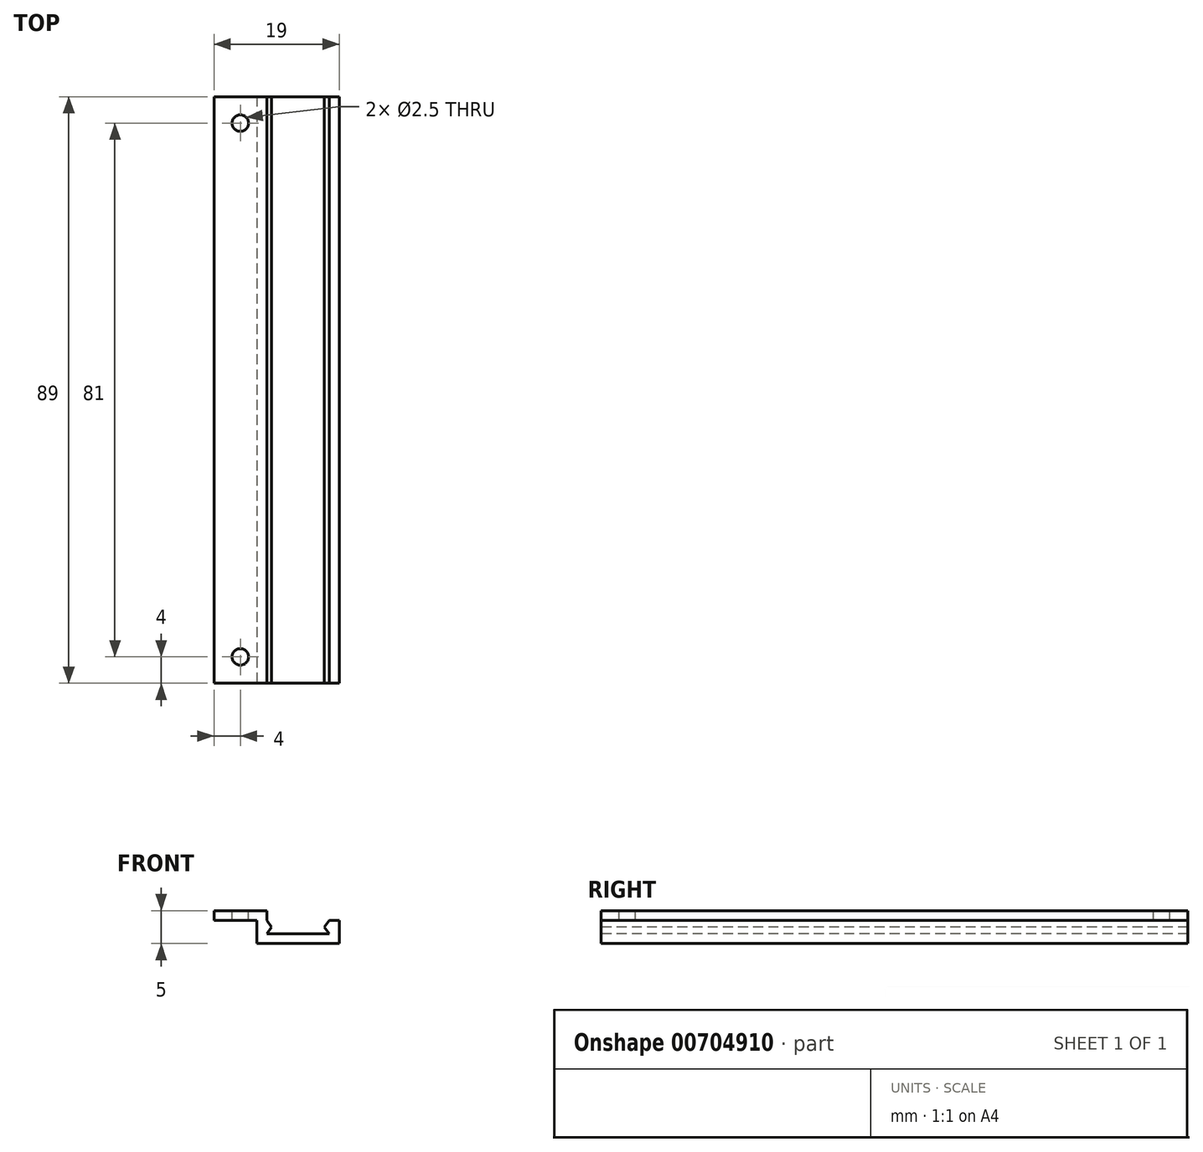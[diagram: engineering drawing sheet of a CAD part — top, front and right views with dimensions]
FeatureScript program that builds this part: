
annotation { "Feature Type Name" : "Feature", "Feature Type Description" : "" }
export const myFeature = defineFeature(function(context is Context, id is Id, definition is map)
    precondition{}
    {
        {
            var Q0;
            Q0=qCreatedBy(makeId("Front.planeOp"),FACE);
            var sketch = newSketch(context, id + "F0", { "sketchPlane" : qUnion([Q0])});
            skLineSegment(sketch, "E0.bottom", {"start": v(4, -0.75) * mm, "end": v(-4, -0.75) * mm});
            skLineSegment(sketch, "E0.top", {"start": v(4, 0.75) * mm, "end": v(-4, 0.75) * mm});
            skLineSegment(sketch, "E0.left", {"start": v(4, -0.75) * mm, "end": v(4, 0.75) * mm});
            skLineSegment(sketch, "E0.right", {"start": v(-4, -0.75) * mm, "end": v(-4, 0.75) * mm});
            skPoint(sketch, "E0.middle", {"position": v(0, 0) * mm});
            skLineSegment(sketch, "E1.bottom", {"start": v(4, 0.75) * mm, "end": v(2.5, 0.75) * mm});
            skLineSegment(sketch, "E1.top", {"start": v(4, -4.25) * mm, "end": v(2.5, -4.25) * mm});
            skLineSegment(sketch, "E1.left", {"start": v(4, 0.75) * mm, "end": v(4, -4.25) * mm});
            skLineSegment(sketch, "E1.right", {"start": v(2.5, 0.75) * mm, "end": v(2.5, -4.25) * mm});
            skLineSegment(sketch, "E2.bottom", {"start": v(2.5, -4.25) * mm, "end": v(15, -4.25) * mm});
            skLineSegment(sketch, "E2.top", {"start": v(2.5, -2.75) * mm, "end": v(15, -2.75) * mm});
            skLineSegment(sketch, "E2.left", {"start": v(2.5, -4.25) * mm, "end": v(2.5, -2.75) * mm});
            skLineSegment(sketch, "E2.right", {"start": v(15, -4.25) * mm, "end": v(15, -2.75) * mm});
            skLineSegment(sketch, "E3.bottom", {"start": v(15, -4.25) * mm, "end": v(13.5, -4.25) * mm});
            skLineSegment(sketch, "E3.top", {"start": v(15, -0.75) * mm, "end": v(13.5, -0.75) * mm});
            skLineSegment(sketch, "E3.left", {"start": v(15, -4.25) * mm, "end": v(15, -0.75) * mm});
            skLineSegment(sketch, "E3.right", {"start": v(13.5, -4.25) * mm, "end": v(13.5, -0.75) * mm});
            skLineSegment(sketch, "E4", {"start": v(4.75, -1.75) * mm, "end": v(4, -2.75) * mm});
            skLineSegment(sketch, "E5", {"start": v(12.75, -1.75) * mm, "end": v(13.5, -2.75) * mm});
            skLineSegment(sketch, "E6.MirrorCS", {"start": v(4.75, -1.75) * mm, "end": v(4, -0.75) * mm});
            skLineSegment(sketch, "E7.MirrorCS", {"start": v(12.75, -1.75) * mm, "end": v(13.5, -0.75) * mm});
            skLineSegment(sketch, "E8", {"start": v(13.5, -0.75) * mm, "end": v(15, -0.75) * mm});
            skSolve(sketch);
        }
        {
            var Q0;
            Q0 = qSketchRegion(id + "F0", true);
            extrude(context, id + "F1", {"entities" : qUnion([Q0]), "oppositeDirection" : true, "depth" : 89 * mm, "offsetDistance" : 25 * mm});
        }
        {
            var Q0;
            Q0=makeQuery(id+"F1.opExtrude","SWEPT_FACE",FACE,{"disambiguationData":[OSD([sQuery(id+"F0.wireOp",EDGE,"E0.top"),sQuery(id+"F0.wireOp",EDGE,"E1.bottom")])]});
            var sketch = newSketch(context, id + "F2", { "sketchPlane" : qUnion([Q0])});
            skCircle(sketch, "E9", {"center": v(0, 4) * mm, "radius": 1.25 * mm});
            skCircle(sketch, "E10", {"center": v(0, 85) * mm, "radius": 1.25 * mm});
            skSolve(sketch);
        }
        {
            var Q0;
            Q0 = qSketchRegion(id + "F2", true);
            extrude(context, id + "F3", {"entities" : qUnion([Q0]), "operationType" : NewBodyOperationType.REMOVE, "oppositeDirection" : true, "depth" : 25 * mm, "offsetDistance" : 25 * mm});
        }
    });
